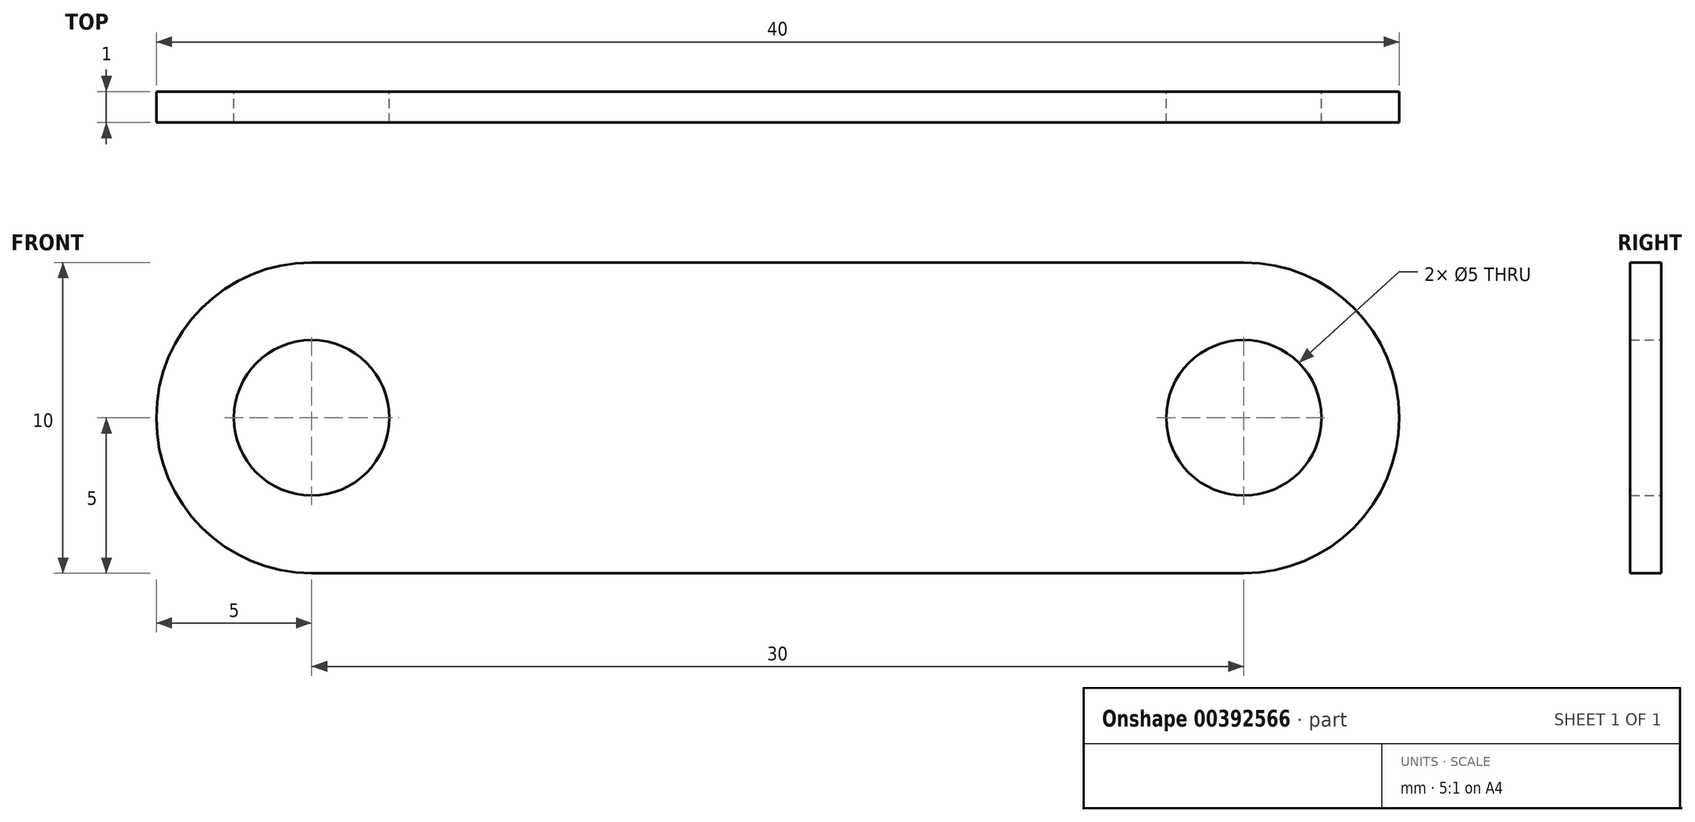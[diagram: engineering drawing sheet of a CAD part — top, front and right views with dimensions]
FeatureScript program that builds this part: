
annotation { "Feature Type Name" : "Feature", "Feature Type Description" : "" }
export const myFeature = defineFeature(function(context is Context, id is Id, definition is map)
    precondition{}
    {
        {
            var Q0;
            Q0=qCreatedBy(makeId("Front.planeOp"),FACE);
            var sketch = newSketch(context, id + "F0", { "sketchPlane" : qUnion([Q0])});
            skLineSegment(sketch, "E0", {"start": v(0, 0) * mm, "end": v(30, 0) * mm, "construction": true});
            skArc(sketch, "E1", {"start": v(30, -5) * mm, "mid": v(35, 0) * mm, "end": v(30, 5) * mm});
            skArc(sketch, "E2", {"start": v(0, 5) * mm, "mid": v(-5, 0) * mm, "end": v(0, -5) * mm});
            skLineSegment(sketch, "E3", {"start": v(0, 5) * mm, "end": v(30, 5) * mm});
            skLineSegment(sketch, "E4", {"start": v(0, -5) * mm, "end": v(30, -5) * mm});
            skCircle(sketch, "E5", {"center": v(30, 0) * mm, "radius": 2.5 * mm});
            skCircle(sketch, "E6", {"center": v(0, 0) * mm, "radius": 2.5 * mm});
            skSolve(sketch);
        }
        {
            var Q0;
            Q0=makeQuery(id+"F0.imprint","IMPRINT",FACE,{"disambiguationData":[TD([[makeQuery(id+"F0.imprint","IMPRINT",EDGE,{"derivedFrom":sQuery(id+"F0.wireOp",EDGE,"E1")}),1.0]])]});
            extrude(context, id + "F1", {"entities" : qUnion([Q0]), "endBound" : BoundingType.SYMMETRIC, "depth" : 1 * mm});
        }
    });
